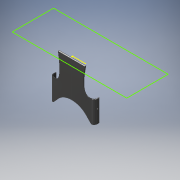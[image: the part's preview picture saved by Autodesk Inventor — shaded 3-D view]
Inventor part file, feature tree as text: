
AUTODESK INVENTOR PART (.ipt)
format: ipt  version: 2019 (Build 230136000, 136)  size: 1,160,192 bytes
history: native  units: mm
features: plane x27, sketch x24, extrude x10, fillet x6, mirror x5, loft x4, chamfer x3, other x1
ambient origin geometry x8: Origin, YZ Plane, XZ Plane, XY Plane, X Axis, Y Axis, Z Axis, Center Point
bodies: Body1 (feature_tree)
feature tree (80):
  sketch  "Sketch1"  dims[d2=55.0mm d5=-107.0mm d13=5.0mm d14=50.0mm]
  plane  "Work Plane1"
  sketch  "Sketch2"  dims[d15=70.0mm d16=5.0mm]
  sketch  "Sketch3"  dims[d17=0.0mm d18=90.0deg d19=0.0mm d20=90.0deg d21=0.0mm d22=90.0deg d23=2.0mm]
  plane  "Work Plane2"
  loft  "Loft2"
  mirror  "Mirror2"
  fillet  "Fillet1"  Radius=5.0mm
  fillet  "Fillet4"  Radius=50.0mm
  plane  "Work Plane3"
  plane  "Work Plane4"
  extrude  "Extrusion1"  Depth=5.0mm
  plane  "Work Plane5"
  extrude  "Extrusion2"  TaperAngle=0.0deg  [1 undecoded]
  fillet  "Fillet5"  [1 undecoded]
  mirror  "Mirror3"
  plane  "Work Plane22"
  plane  "Work Plane6"
  plane  "Work Plane7"
  fillet  "Fillet11"  Radius=2.0mm
  extrude  "Extrusion7"  Depth=87.5mm
  mirror  "Mirror4"
  plane  "Work Plane8"
  plane  "Work Plane9"
  sketch  "Sketch20"  dims[d42=2.0mm]
  plane  "Work Plane10"
  sketch  "Sketch21"  dims[d43=2.0mm]
  plane  "Work Plane11"
  sketch  "Sketch22"  dims[d44=2.0mm]
  loft  "Loft5"
  plane  "Work Plane13"
  sketch  "Sketch25"  dims[d45=2.0mm]
  plane  "Work Plane18"
  loft  "Loft6"
  mirror  "Mirror5"
  plane  "Work Plane19"
  extrude  "Extrusion9"  Depth=2.0mm
  fillet  "Fillet12"  Radius=2.0mm
  fillet  "Fillet14"  Radius=2.0mm
  plane  "Work Plane20"
  plane  "Work Plane21"
  plane  "Work Plane23"
  plane  "Work Plane24"
  plane  "Work Plane25"
  sketch  "Sketch33"  dims[d48=2.0mm]
  plane  "Work Plane26"
  sketch  "Sketch34"  dims[d49=2.0mm d50=2.0mm d51=1.0mm]
  plane  "Work Plane27"
  sketch  "Sketch35"  dims[d79=-25.0mm]
  plane  "Work Plane30"
  sketch  "Sketch38"  dims[d84=2.0mm]
  plane  "Work Plane31"
  plane  "Work Plane35"
  chamfer  "Chamfer7"  Distance=2.0mm
  chamfer  "Chamfer8"  Distance=28.0mm
  chamfer  "Chamfer9"  Distance=22.0mm
  loft  "Loft10"
  mirror  "Mirror9"
  plane  "Work Plane37"
  sketch  "Sketch47"  dims[d85=13.5mm]
  extrude  "Extrusion25"  Depth=70.0mm
  extrude  "Extrusion26"  Depth=3.0mm
  extrude  "Extrusion27"  Depth=20.0mm
  plane  "Work Plane38"
  extrude  "Extrusion28"  TaperAngle=0.0deg  [1 undecoded]
  extrude  "Extrusion29"  TaperAngle=0.0deg  [1 undecoded]
  extrude  "Extrusion30"  TaperAngle=0.0deg  [1 undecoded]
  sketch  "Sketch4"  dims[d29=1.0mm d30=-4.5mm d31=87.5mm]
  sketch  "Sketch5"  dims[d32=0.0mm d33=0.0mm d34=-28.0mm]
  sketch  "Sketch6"  dims[d35=15.0mm d36=3.0mm]
  sketch  "Sketch17"  dims[d37=0.0mm d38=0.0mm d39=2.0mm d40=2.0mm d41=2.0mm]
  sketch  "Sketch27"  dims[d46=2.0mm]
  other  "Edges1"
  sketch  "Sketch28"  dims[d47=2.0mm]
  sketch  "Sketch48"  dims[d86=2.5mm]
  sketch  "Sketch49"  dims[d87=5.0mm]
  sketch  "Sketch50"  dims[d88=6.25mm d89=28.0mm d90=0.0mm d91=22.0mm d101=200.0mm]
  sketch  "Sketch51"  dims[d104=5.0mm d105=50.0mm d106=-80.0mm d107=45.0mm]
  sketch  "Sketch52"  dims[d108=3.0mm d109=70.0mm]
  sketch  "Sketch53"  dims[d110=80.0mm d111=3.0mm d112=20.0mm d123=0.0mm d124=90.0deg d125=0.0mm d126=90.0deg d127=0.0mm d128=90.0deg d129=-20.0mm d131=2.0mm d132=80.0mm d133=8.0mm d134=0.0mm d135=0.0mm d136=90.0deg d137=0.0mm d138=90.0deg d139=0.0mm d140=90.0deg d141=3.0mm d142=7.0mm d143=10.0mm d144=0.0mm d145=70.0mm d147=10.0mm d171=35.75mm d174=-8.25mm d177=20.0mm d179=30.0mm d180=5.0mm d181=41.5mm d182=15.0mm d183=10.0mm d184=5.0mm d200=-2.0mm d219=15.0mm d241=2.0mm d242=2.0mm d243=45.0deg d244=1.0mm d245=2.0mm d246=45.0deg d247=0.5mm d248=2.0mm d249=45.0deg d250=5.0mm d251=0.0mm d252=90.0deg d253=0.0mm d254=90.0deg d255=0.0mm d256=90.0deg d263=10.0mm d264=0.0mm d265=5.0mm d266=0.0mm d267=4.0mm d268=20.0mm d269=0.0mm d270=16.0mm d271=14.0mm d272=20.0mm d273=0.0mm d274=4.0mm d275=20.0mm d276=0.0mm d277=0.0mm d278=0.0mm]
note: 5 required parameter values undecoded (feature->parameter linkage not recoverable at this tier; creation-order binding heuristic only, values carry confidence <= 0.55)
